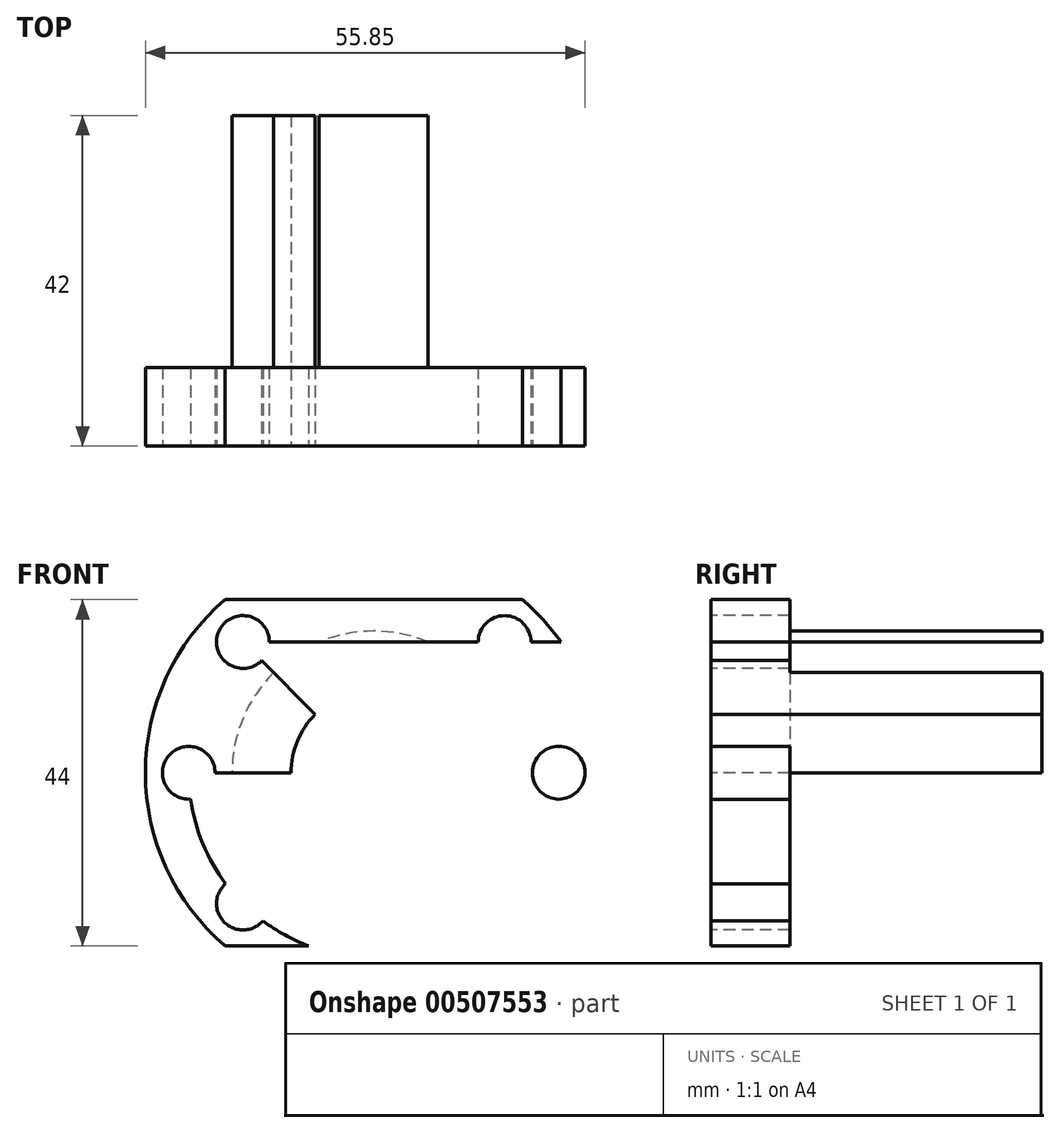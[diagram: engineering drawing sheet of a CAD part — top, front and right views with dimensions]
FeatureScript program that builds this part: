
annotation { "Feature Type Name" : "Feature", "Feature Type Description" : "" }
export const myFeature = defineFeature(function(context is Context, id is Id, definition is map)
    precondition{}
    {
        {
            var Q0;
            Q0=qCreatedBy(makeId("Front.planeOp"),FACE);
            var sketch = newSketch(context, id + "F0", { "sketchPlane" : qUnion([Q0])});
            skCircle(sketch, "E0", {"center": v(0, 0) * mm, "radius": 18 * mm});
            skSolve(sketch);
        }
        {
            var Q0;
            Q0 = qSketchRegion(id + "F0", true);
            extrude(context, id + "F1", {"entities" : qUnion([Q0]), "depth" : 32 * mm, "offsetDistance" : 25 * mm});
        }
        {
            var Q0;
            Q0=makeQuery(id+"F1.opExtrude","CAP_FACE",FACE,{"disambiguationData":[OSD([sQuery(id+"F0.wireOp",EDGE,"E0")])],"isStart":false});
            var sketch = newSketch(context, id + "F2", { "sketchPlane" : qUnion([Q0])});
            skCircle(sketch, "E1", {"center": v(0, 0) * mm, "radius": 29 * mm});
            skSolve(sketch);
        }
        {
            var Q0;
            Q0 = qSketchRegion(id + "F2", true);
            extrude(context, id + "F3", {"entities" : qUnion([Q0]), "operationType" : NewBodyOperationType.ADD, "depth" : 10 * mm, "offsetDistance" : 25 * mm});
        }
        {
            var Q0;
            Q0=makeQuery(id+"F3.opExtrude","CAP_FACE",FACE,{"disambiguationData":[OSD([sQuery(id+"F2.wireOp",EDGE,"E1")])],"isStart":false});
            var sketch = newSketch(context, id + "F4", { "sketchPlane" : qUnion([Q0])});
            skCircle(sketch, "E2", {"center": v(0, 0) * mm, "radius": 10.5 * mm});
            skCircle(sketch, "E3", {"center": v(0, 0) * mm, "radius": 23.5 * mm});
            skCircle(sketch, "E4", {"center": v(23.5, 0) * mm, "radius": 3.35 * mm});
            skCircle(sketch, "E5", {"center": v(-23.5, 0) * mm, "radius": 3.35 * mm});
            skCircle(sketch, "E6", {"center": v(-16.62, 16.62) * mm, "radius": 3.35 * mm});
            skCircle(sketch, "E7", {"center": v(16.62, 16.62) * mm, "radius": 3.35 * mm});
            skCircle(sketch, "E8", {"center": v(16.62, -16.62) * mm, "radius": 3.35 * mm});
            skLineSegment(sketch, "E9", {"start": v(-23.5, 0) * mm, "end": v(0, 0) * mm});
            skLineSegment(sketch, "E10", {"start": v(0, 0) * mm, "end": v(-24.34, 24.34) * mm});
            skLineSegment(sketch, "E11", {"start": v(-16.62, 16.62) * mm, "end": v(26.28, 16.62) * mm});
            skCircle(sketch, "E12", {"center": v(-16.62, -16.62) * mm, "radius": 3.35 * mm});
            skLineSegment(sketch, "E13.bottom", {"start": v(-35, -22) * mm, "end": v(35, -22) * mm});
            skLineSegment(sketch, "E13.top", {"start": v(-35, 22) * mm, "end": v(35, 22) * mm});
            skLineSegment(sketch, "E13.left", {"start": v(-35, -22) * mm, "end": v(-35, 22) * mm});
            skLineSegment(sketch, "E13.right", {"start": v(35, -22) * mm, "end": v(35, 22) * mm});
            skSolve(sketch);
        }
        {
            var Q0;
            {var subQ0=sQuery(id+"F4.wireOp",EDGE,"E9");var subQ1=sQuery(id+"F4.wireOp",EDGE,"E2");var subQ2=makeQuery(id+"F4.imprint","INTERSECT",VERTEX,{"derivedFrom":[subQ1,subQ0]});Q0=makeQuery(id+"F4.imprint","IMPRINT",FACE,{"disambiguationData":[TD([[makeQuery(id+"F4.imprint","IMPRINT",EDGE,{"disambiguationData":[TD([[subQ2,1.0]])],"derivedFrom":subQ1}),1.0]])]});}
            var Q1;
            {var subQ0=sQuery(id+"F4.wireOp",EDGE,"E9");var subQ1=sQuery(id+"F4.wireOp",EDGE,"E2");var subQ2=makeQuery(id+"F4.imprint","INTERSECT",VERTEX,{"derivedFrom":[subQ1,subQ0]});Q1=makeQuery(id+"F4.imprint","IMPRINT",FACE,{"disambiguationData":[TD([[makeQuery(id+"F4.imprint","IMPRINT",EDGE,{"disambiguationData":[TD([[subQ2,-1.0]])],"derivedFrom":subQ1}),1.0]])]});}
            var Q2;
            {var subQ0=sQuery(id+"F4.wireOp",EDGE,"E11");var subQ1=sQuery(id+"F4.wireOp",EDGE,"E6");var subQ2=makeQuery(id+"F4.imprint","INTERSECT",VERTEX,{"derivedFrom":[subQ1,subQ0]});Q2=makeQuery(id+"F4.imprint","IMPRINT",FACE,{"disambiguationData":[TD([[makeQuery(id+"F4.imprint","IMPRINT",EDGE,{"disambiguationData":[TD([[subQ2,1.0]])],"derivedFrom":subQ1}),1.0]])]});}
            var Q3;
            {var subQ1=sQuery(id+"F4.wireOp",EDGE,"E3");var subQ3=sQuery(id+"F4.wireOp",EDGE,"E6");var subQ4=makeQuery(id+"F4.imprint","INTERSECT",VERTEX,{"disambiguationData":[OD(1.0)],"derivedFrom":[subQ1,subQ3]});Q3=makeQuery(id+"F4.imprint","IMPRINT",FACE,{"disambiguationData":[TD([[makeQuery(id+"F4.imprint","IMPRINT",EDGE,{"disambiguationData":[TD([[subQ4,-1.0]])],"derivedFrom":subQ3}),1.0]])]});}
            var Q4;
            {var subQ1=sQuery(id+"F4.wireOp",EDGE,"E3");var subQ3=sQuery(id+"F4.wireOp",EDGE,"E6");var subQ4=makeQuery(id+"F4.imprint","INTERSECT",VERTEX,{"disambiguationData":[OD(1.0)],"derivedFrom":[subQ1,subQ3]});Q4=makeQuery(id+"F4.imprint","IMPRINT",FACE,{"disambiguationData":[TD([[makeQuery(id+"F4.imprint","IMPRINT",EDGE,{"disambiguationData":[TD([[subQ4,1.0]])],"derivedFrom":subQ3}),1.0]])]});}
            var Q5;
            {var subQ1=sQuery(id+"F4.wireOp",EDGE,"E3");var subQ3=sQuery(id+"F4.wireOp",EDGE,"E6");var subQ4=makeQuery(id+"F4.imprint","INTERSECT",VERTEX,{"disambiguationData":[OD(0.0)],"derivedFrom":[subQ1,subQ3]});Q5=makeQuery(id+"F4.imprint","IMPRINT",FACE,{"disambiguationData":[TD([[makeQuery(id+"F4.imprint","IMPRINT",EDGE,{"disambiguationData":[TD([[subQ4,-1.0]])],"derivedFrom":subQ3}),1.0]])]});}
            var Q6;
            {var subQ0=sQuery(id+"F4.wireOp",EDGE,"E3");var subQ1=makeQuery(id+"F4.imprint","INTERSECT",VERTEX,{"derivedFrom":[subQ0,sQuery(id+"F4.wireOp",EDGE,"E9")]});Q6=makeQuery(id+"F4.imprint","IMPRINT",FACE,{"disambiguationData":[TD([[makeQuery(id+"F4.imprint","IMPRINT",EDGE,{"disambiguationData":[TD([[subQ1,1.0]])],"derivedFrom":subQ0}),-1.0]])]});}
            var Q7;
            {var subQ0=sQuery(id+"F4.wireOp",EDGE,"E9");var subQ1=sQuery(id+"F4.wireOp",EDGE,"E3");var subQ2=makeQuery(id+"F4.imprint","INTERSECT",VERTEX,{"derivedFrom":[subQ1,subQ0]});Q7=makeQuery(id+"F4.imprint","IMPRINT",FACE,{"disambiguationData":[TD([[makeQuery(id+"F4.imprint","IMPRINT",EDGE,{"disambiguationData":[TD([[subQ2,1.0]])],"derivedFrom":subQ1}),1.0]])]});}
            var Q8;
            {var subQ0=sQuery(id+"F4.wireOp",EDGE,"E9");var subQ1=sQuery(id+"F4.wireOp",EDGE,"E3");var subQ2=makeQuery(id+"F4.imprint","INTERSECT",VERTEX,{"derivedFrom":[subQ1,subQ0]});Q8=makeQuery(id+"F4.imprint","IMPRINT",FACE,{"disambiguationData":[TD([[makeQuery(id+"F4.imprint","IMPRINT",EDGE,{"disambiguationData":[TD([[subQ2,-1.0]])],"derivedFrom":subQ1}),1.0]])]});}
            var Q9;
            {var subQ0=sQuery(id+"F4.wireOp",EDGE,"E12");var subQ1=sQuery(id+"F4.wireOp",EDGE,"E3");var subQ2=makeQuery(id+"F4.imprint","INTERSECT",VERTEX,{"disambiguationData":[OD(0.0)],"derivedFrom":[subQ1,subQ0]});Q9=makeQuery(id+"F4.imprint","IMPRINT",FACE,{"disambiguationData":[TD([[makeQuery(id+"F4.imprint","IMPRINT",EDGE,{"disambiguationData":[TD([[subQ2,-1.0]])],"derivedFrom":subQ1}),-1.0]])]});}
            var Q10;
            {var subQ0=sQuery(id+"F4.wireOp",EDGE,"E12");var subQ1=sQuery(id+"F4.wireOp",EDGE,"E3");var subQ2=makeQuery(id+"F4.imprint","INTERSECT",VERTEX,{"disambiguationData":[OD(0.0)],"derivedFrom":[subQ1,subQ0]});Q10=makeQuery(id+"F4.imprint","IMPRINT",FACE,{"disambiguationData":[TD([[makeQuery(id+"F4.imprint","IMPRINT",EDGE,{"disambiguationData":[TD([[subQ2,-1.0]])],"derivedFrom":subQ1}),1.0]])]});}
            var Q11;
            {var subQ0=sQuery(id+"F4.wireOp",EDGE,"E8");var subQ1=sQuery(id+"F4.wireOp",EDGE,"E3");var subQ2=makeQuery(id+"F4.imprint","INTERSECT",VERTEX,{"disambiguationData":[OD(0.0)],"derivedFrom":[subQ1,subQ0]});Q11=makeQuery(id+"F4.imprint","IMPRINT",FACE,{"disambiguationData":[TD([[makeQuery(id+"F4.imprint","IMPRINT",EDGE,{"disambiguationData":[TD([[subQ2,-1.0]])],"derivedFrom":subQ1}),1.0]])]});}
            var Q12;
            {var subQ0=sQuery(id+"F4.wireOp",EDGE,"E8");var subQ1=sQuery(id+"F4.wireOp",EDGE,"E3");var subQ2=makeQuery(id+"F4.imprint","INTERSECT",VERTEX,{"disambiguationData":[OD(0.0)],"derivedFrom":[subQ1,subQ0]});Q12=makeQuery(id+"F4.imprint","IMPRINT",FACE,{"disambiguationData":[TD([[makeQuery(id+"F4.imprint","IMPRINT",EDGE,{"disambiguationData":[TD([[subQ2,-1.0]])],"derivedFrom":subQ1}),-1.0]])]});}
            var Q13;
            {var subQ0=sQuery(id+"F4.wireOp",EDGE,"E4");var subQ1=sQuery(id+"F4.wireOp",EDGE,"E3");var subQ2=makeQuery(id+"F4.imprint","INTERSECT",VERTEX,{"disambiguationData":[OD(0.0)],"derivedFrom":[subQ1,subQ0]});Q13=makeQuery(id+"F4.imprint","IMPRINT",FACE,{"disambiguationData":[TD([[makeQuery(id+"F4.imprint","IMPRINT",EDGE,{"disambiguationData":[TD([[subQ2,1.0]])],"derivedFrom":subQ1}),1.0]])]});}
            var Q14;
            {var subQ0=sQuery(id+"F4.wireOp",EDGE,"E4");var subQ1=sQuery(id+"F4.wireOp",EDGE,"E3");var subQ2=makeQuery(id+"F4.imprint","INTERSECT",VERTEX,{"disambiguationData":[OD(0.0)],"derivedFrom":[subQ1,subQ0]});Q14=makeQuery(id+"F4.imprint","IMPRINT",FACE,{"disambiguationData":[TD([[makeQuery(id+"F4.imprint","IMPRINT",EDGE,{"disambiguationData":[TD([[subQ2,1.0]])],"derivedFrom":subQ1}),-1.0]])]});}
            var Q15;
            {var subQ0=sQuery(id+"F4.wireOp",EDGE,"E11");var subQ1=sQuery(id+"F4.wireOp",EDGE,"E3");var subQ2=makeQuery(id+"F4.imprint","INTERSECT",VERTEX,{"derivedFrom":[subQ1,subQ0]});Q15=makeQuery(id+"F4.imprint","IMPRINT",FACE,{"disambiguationData":[TD([[makeQuery(id+"F4.imprint","IMPRINT",EDGE,{"disambiguationData":[TD([[subQ2,-1.0]])],"derivedFrom":subQ1}),-1.0]])]});}
            var Q16;
            {var subQ0=sQuery(id+"F4.wireOp",EDGE,"E7");var subQ1=sQuery(id+"F4.wireOp",EDGE,"E3");var subQ2=makeQuery(id+"F4.imprint","INTERSECT",VERTEX,{"disambiguationData":[OD(0.0)],"derivedFrom":[subQ1,subQ0]});Q16=makeQuery(id+"F4.imprint","IMPRINT",FACE,{"disambiguationData":[TD([[makeQuery(id+"F4.imprint","IMPRINT",EDGE,{"disambiguationData":[TD([[subQ2,-1.0]])],"derivedFrom":subQ1}),-1.0]])]});}
            var Q17;
            {var subQ0=sQuery(id+"F4.wireOp",EDGE,"E7");var subQ1=sQuery(id+"F4.wireOp",EDGE,"E3");var subQ2=makeQuery(id+"F4.imprint","INTERSECT",VERTEX,{"disambiguationData":[OD(0.0)],"derivedFrom":[subQ1,subQ0]});Q17=makeQuery(id+"F4.imprint","IMPRINT",FACE,{"disambiguationData":[TD([[makeQuery(id+"F4.imprint","IMPRINT",EDGE,{"disambiguationData":[TD([[subQ2,-1.0]])],"derivedFrom":subQ1}),1.0]])]});}
            var Q18;
            {var subQ0=sQuery(id+"F4.wireOp",EDGE,"E11");var subQ1=sQuery(id+"F4.wireOp",EDGE,"E3");var subQ2=makeQuery(id+"F4.imprint","INTERSECT",VERTEX,{"derivedFrom":[subQ1,subQ0]});Q18=makeQuery(id+"F4.imprint","IMPRINT",FACE,{"disambiguationData":[TD([[makeQuery(id+"F4.imprint","IMPRINT",EDGE,{"disambiguationData":[TD([[subQ2,-1.0]])],"derivedFrom":subQ1}),1.0]])]});}
            var Q19;
            {var subQ0=sQuery(id+"F4.wireOp",EDGE,"E13.top");var subQ1=sQuery(id+"F4.wireOp",EDGE,"E3");var subQ2=makeQuery(id+"F4.imprint","INTERSECT",VERTEX,{"disambiguationData":[OD(0.0)],"derivedFrom":[subQ1,subQ0]});Q19=makeQuery(id+"F4.imprint","IMPRINT",FACE,{"disambiguationData":[TD([[makeQuery(id+"F4.imprint","IMPRINT",EDGE,{"disambiguationData":[TD([[subQ2,-1.0]])],"derivedFrom":subQ1}),-1.0]])]});}
            var Q20;
            {var subQ0=sQuery(id+"F4.wireOp",EDGE,"E13.top");var subQ1=sQuery(id+"F4.wireOp",EDGE,"E3");var subQ2=makeQuery(id+"F4.imprint","INTERSECT",VERTEX,{"disambiguationData":[OD(0.0)],"derivedFrom":[subQ1,subQ0]});Q20=makeQuery(id+"F4.imprint","IMPRINT",FACE,{"disambiguationData":[TD([[makeQuery(id+"F4.imprint","IMPRINT",EDGE,{"disambiguationData":[TD([[subQ2,-1.0]])],"derivedFrom":subQ1}),1.0]])]});}
            var Q21;
            {var subQ0=sQuery(id+"F4.wireOp",EDGE,"E13.bottom");var subQ1=sQuery(id+"F4.wireOp",EDGE,"E3");var subQ2=makeQuery(id+"F4.imprint","INTERSECT",VERTEX,{"disambiguationData":[OD(0.0)],"derivedFrom":[subQ1,subQ0]});Q21=makeQuery(id+"F4.imprint","IMPRINT",FACE,{"disambiguationData":[TD([[makeQuery(id+"F4.imprint","IMPRINT",EDGE,{"disambiguationData":[TD([[subQ2,-1.0]])],"derivedFrom":subQ1}),-1.0]])]});}
            var Q22;
            {var subQ0=sQuery(id+"F4.wireOp",EDGE,"E13.bottom");var subQ1=sQuery(id+"F4.wireOp",EDGE,"E3");var subQ2=makeQuery(id+"F4.imprint","INTERSECT",VERTEX,{"disambiguationData":[OD(0.0)],"derivedFrom":[subQ1,subQ0]});Q22=makeQuery(id+"F4.imprint","IMPRINT",FACE,{"disambiguationData":[TD([[makeQuery(id+"F4.imprint","IMPRINT",EDGE,{"disambiguationData":[TD([[subQ2,-1.0]])],"derivedFrom":subQ1}),1.0]])]});}
            var Q23;
            {var subQ1=sQuery(id+"F4.wireOp",EDGE,"E3");var subQ3=sQuery(id+"F4.wireOp",EDGE,"E6");var subQ4=makeQuery(id+"F4.imprint","INTERSECT",VERTEX,{"disambiguationData":[OD(0.0)],"derivedFrom":[subQ1,subQ3]});Q23=makeQuery(id+"F4.imprint","IMPRINT",FACE,{"disambiguationData":[TD([[makeQuery(id+"F4.imprint","IMPRINT",EDGE,{"disambiguationData":[TD([[subQ4,1.0]])],"derivedFrom":subQ3}),1.0]])]});}
            extrude(context, id + "F5", {"entities" : qUnion([Q0, Q1, Q2, Q3, Q4, Q5, Q6, Q7, Q8, Q9, Q10, Q11, Q12, Q13, Q14, Q15, Q16, Q17, Q18, Q19, Q20, Q21, Q22, Q23]), "operationType" : NewBodyOperationType.REMOVE, "oppositeDirection" : true, "depth" : 42 * mm, "offsetDistance" : 25 * mm});
        }
    });
